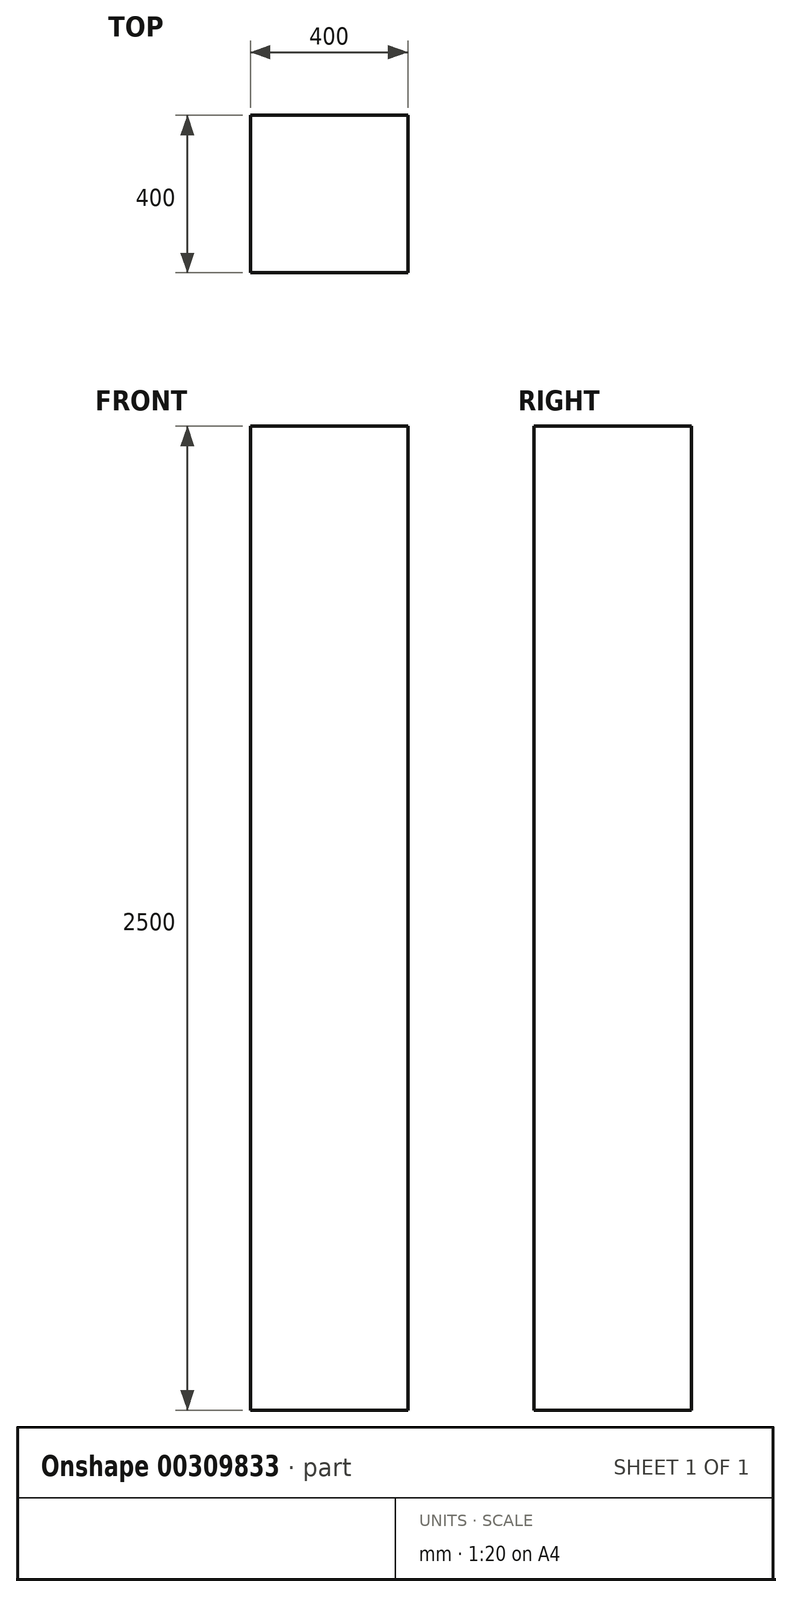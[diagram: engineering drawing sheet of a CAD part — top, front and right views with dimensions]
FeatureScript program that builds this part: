
annotation { "Feature Type Name" : "Feature", "Feature Type Description" : "" }
export const myFeature = defineFeature(function(context is Context, id is Id, definition is map)
    precondition{}
    {
        {
            var Q0;
            Q0=qCreatedBy(makeId("Front.planeOp"),FACE);
            var sketch = newSketch(context, id + "F0", { "sketchPlane" : qUnion([Q0])});
            skLineSegment(sketch, "E0.bottom", {"start": v(-807.42, 1252.21) * mm, "end": v(-407.42, 1252.21) * mm});
            skLineSegment(sketch, "E0.top", {"start": v(-807.42, -1247.79) * mm, "end": v(-407.42, -1247.79) * mm});
            skLineSegment(sketch, "E0.left", {"start": v(-807.42, 1252.21) * mm, "end": v(-807.42, -1247.79) * mm});
            skLineSegment(sketch, "E0.right", {"start": v(-407.42, 1252.21) * mm, "end": v(-407.42, -1247.79) * mm});
            skSolve(sketch);
        }
        {
            var Q0;
            Q0 = qSketchRegion(id + "F0", true);
            extrude(context, id + "F1", {"entities" : qUnion([Q0]), "depth" : 400 * mm});
        }
    });
